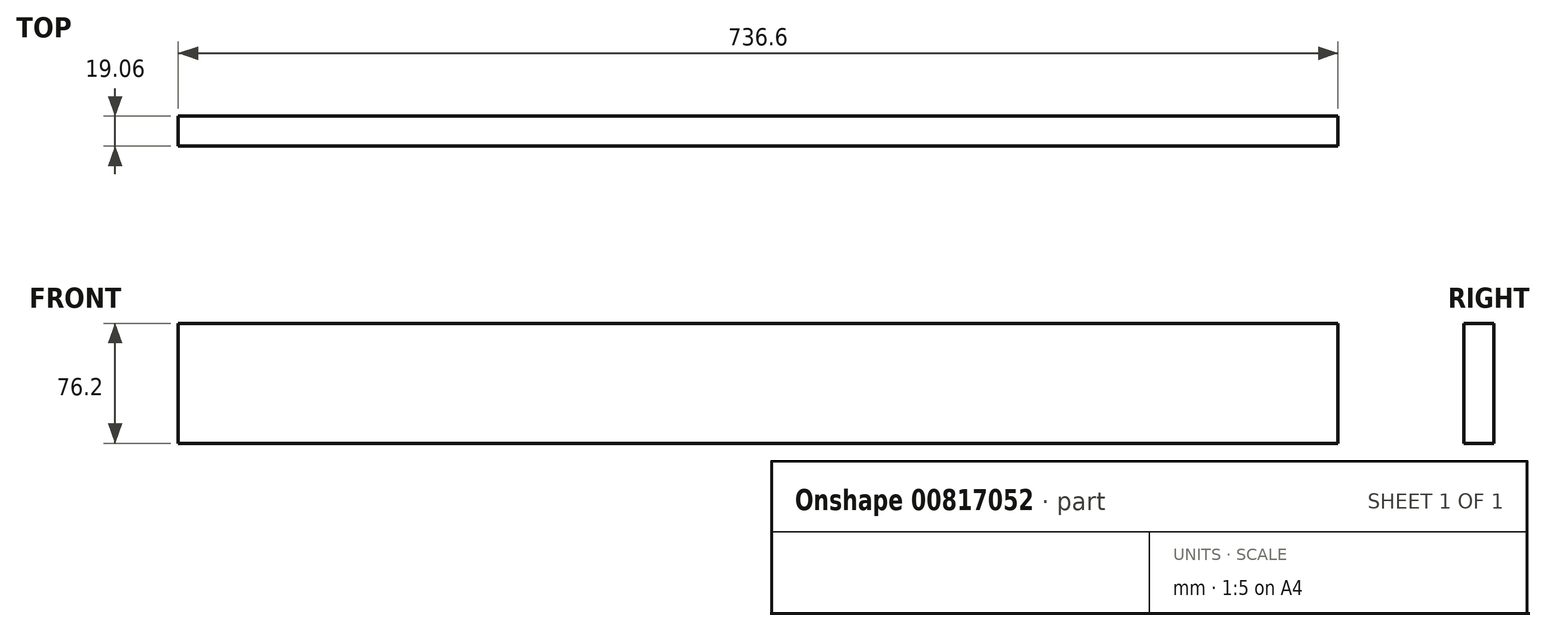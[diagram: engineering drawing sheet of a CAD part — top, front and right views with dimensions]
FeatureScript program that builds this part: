
annotation { "Feature Type Name" : "Feature", "Feature Type Description" : "" }
export const myFeature = defineFeature(function(context is Context, id is Id, definition is map)
    precondition{}
    {
        {
            var Q0;
            Q0=qCreatedBy(makeId("Right.planeOp"),FACE);
            var sketch = newSketch(context, id + "F0", { "sketchPlane" : qUnion([Q0])});
            skLineSegment(sketch, "E0.bottom", {"start": v(9.53, 38.1) * mm, "end": v(-9.53, 38.1) * mm});
            skLineSegment(sketch, "E0.top", {"start": v(9.53, -38.1) * mm, "end": v(-9.53, -38.1) * mm});
            skLineSegment(sketch, "E0.left", {"start": v(9.53, 38.1) * mm, "end": v(9.53, -38.1) * mm});
            skLineSegment(sketch, "E0.right", {"start": v(-9.53, 38.1) * mm, "end": v(-9.53, -38.1) * mm});
            skPoint(sketch, "E0.middle", {"position": v(0, 0) * mm});
            skSolve(sketch);
        }
        {
            var Q0;
            Q0=qSketchRegion(id+"F0",true);
            extrude(context, id + "F1", {"entities" : qUnion([Q0]), "depth" : 736.6 * mm, "offsetDistance" : 25.4 * mm});
        }
    });
